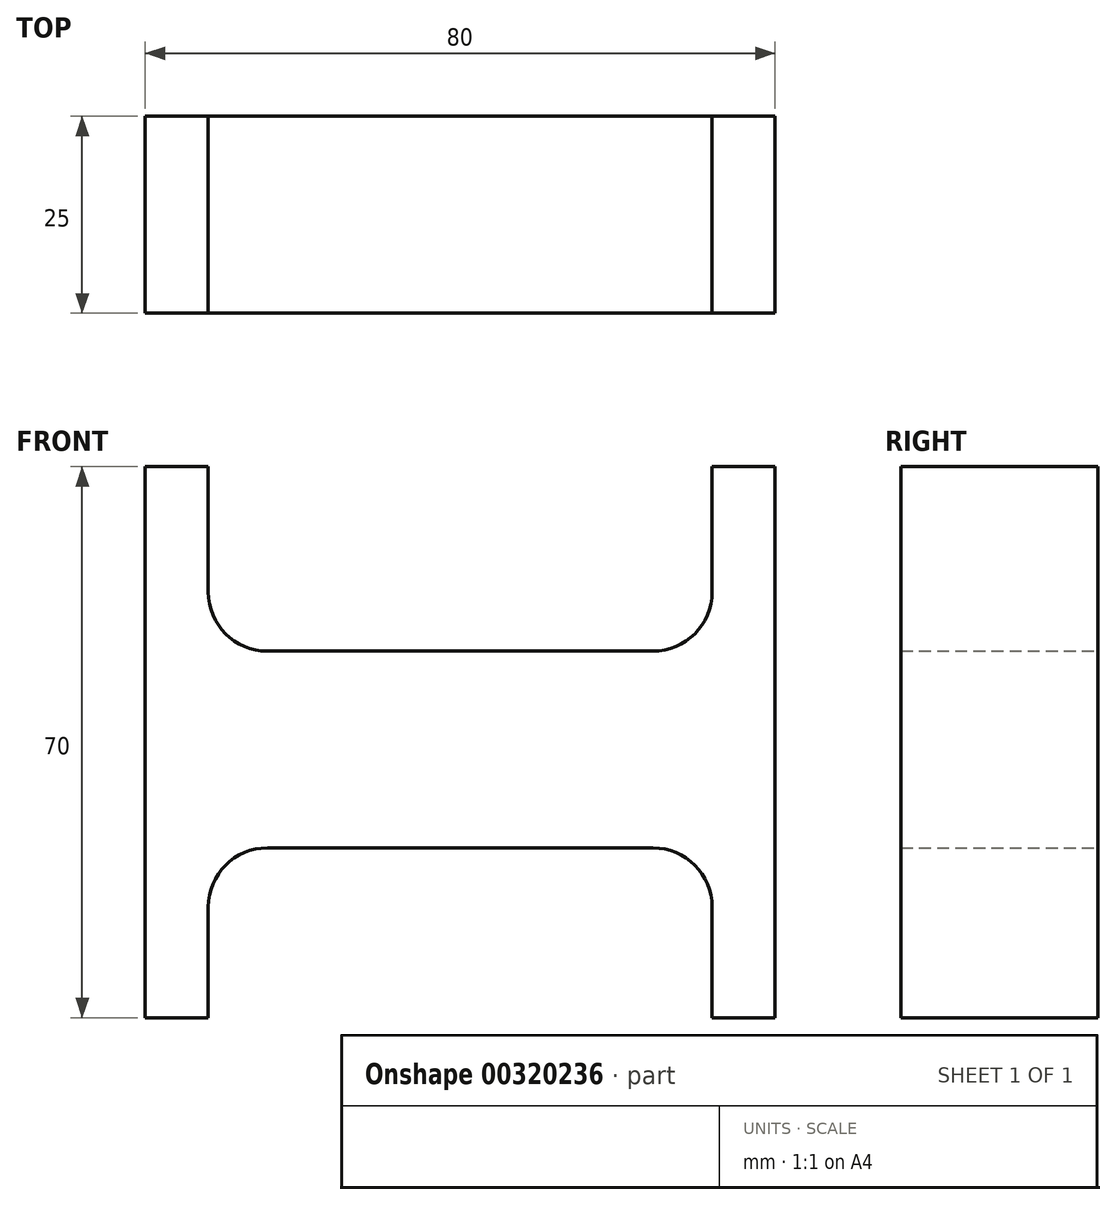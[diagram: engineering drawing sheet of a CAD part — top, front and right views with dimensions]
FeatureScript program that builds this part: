
annotation { "Feature Type Name" : "Feature", "Feature Type Description" : "" }
export const myFeature = defineFeature(function(context is Context, id is Id, definition is map)
    precondition{}
    {
        {
            var Q0;
            Q0=qCreatedBy(makeId("Front.planeOp"),FACE);
            var sketch = newSketch(context, id + "F0", { "sketchPlane" : qUnion([Q0])});
            skLineSegment(sketch, "E0", {"start": v(-39.34, 35.94) * mm, "end": v(-39.34, -34.06) * mm});
            skLineSegment(sketch, "E1", {"start": v(-39.34, -34.06) * mm, "end": v(-31.34, -34.06) * mm});
            skLineSegment(sketch, "E2", {"start": v(-31.34, -34.06) * mm, "end": v(-31.34, -20) * mm});
            skLineSegment(sketch, "E3", {"start": v(-23.84, -12.5) * mm, "end": v(25.16, -12.5) * mm});
            skLineSegment(sketch, "E4", {"start": v(32.66, -20) * mm, "end": v(32.66, -34.06) * mm});
            skLineSegment(sketch, "E5", {"start": v(32.66, -34.06) * mm, "end": v(40.66, -34.06) * mm});
            skLineSegment(sketch, "E6", {"start": v(40.66, -34.06) * mm, "end": v(40.66, 35.94) * mm});
            skLineSegment(sketch, "E7", {"start": v(40.66, 35.94) * mm, "end": v(32.66, 35.94) * mm});
            skLineSegment(sketch, "E8", {"start": v(32.66, 35.94) * mm, "end": v(32.66, 20) * mm});
            skLineSegment(sketch, "E9", {"start": v(25.16, 12.5) * mm, "end": v(-23.84, 12.5) * mm});
            skLineSegment(sketch, "E10", {"start": v(-31.34, 20) * mm, "end": v(-31.34, 35.94) * mm});
            skLineSegment(sketch, "E11", {"start": v(-31.34, 35.94) * mm, "end": v(-39.34, 35.94) * mm});
            skPoint(sketch, "E12.visualSharp", {"position": v(-31.34, 12.5) * mm});
            skArc(sketch, "E12.filletArc", {"start": v(-31.34, 20) * mm, "mid": v(-29.14, 14.7) * mm, "end": v(-23.84, 12.5) * mm});
            skPoint(sketch, "E13.visualSharp", {"position": v(-31.34, -12.5) * mm});
            skArc(sketch, "E13.filletArc", {"start": v(-23.84, -12.5) * mm, "mid": v(-29.14, -14.7) * mm, "end": v(-31.34, -20) * mm});
            skPoint(sketch, "E14.visualSharp", {"position": v(32.66, -12.5) * mm});
            skArc(sketch, "E14.filletArc", {"start": v(32.66, -20) * mm, "mid": v(30.47, -14.7) * mm, "end": v(25.16, -12.5) * mm});
            skPoint(sketch, "E15.visualSharp", {"position": v(32.66, 12.5) * mm});
            skArc(sketch, "E15.filletArc", {"start": v(25.16, 12.5) * mm, "mid": v(30.47, 14.7) * mm, "end": v(32.66, 20) * mm});
            skSolve(sketch);
        }
        {
            var Q0;
            Q0=makeQuery(id+"F0.imprint","IMPRINT",FACE,{"disambiguationData":[TD([[makeQuery(id+"F0.imprint","IMPRINT",EDGE,{"derivedFrom":sQuery(id+"F0.wireOp",EDGE,"E0")}),1.0]])]});
            extrude(context, id + "F1", {"entities" : qUnion([Q0]), "depth" : 25 * mm});
        }
    });
